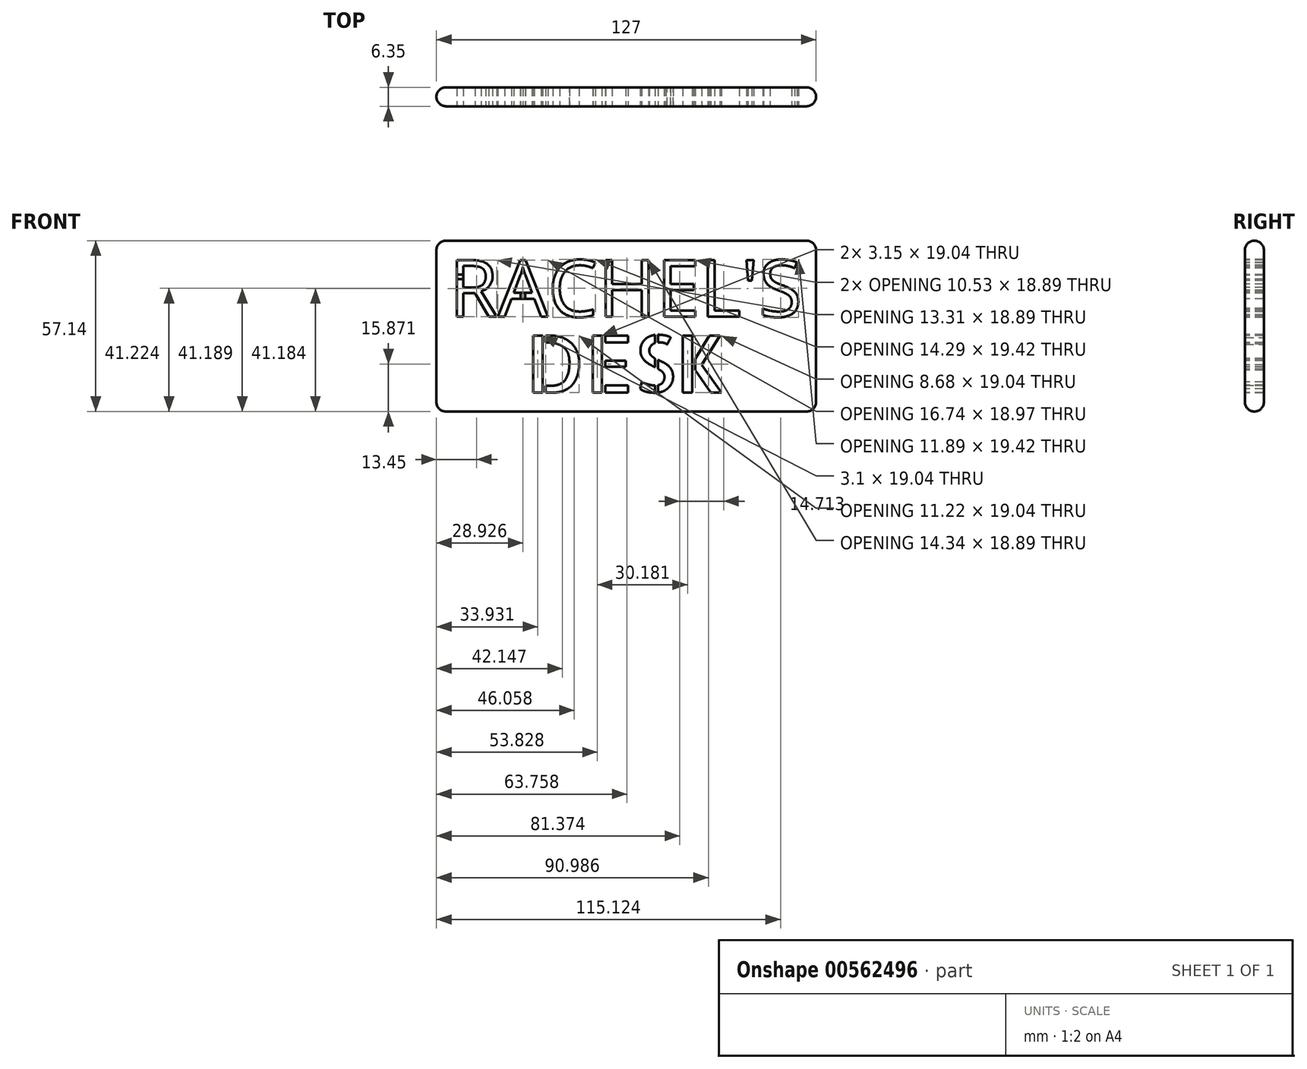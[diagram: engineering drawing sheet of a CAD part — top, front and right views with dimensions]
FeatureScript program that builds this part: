
annotation { "Feature Type Name" : "Feature", "Feature Type Description" : "" }
export const myFeature = defineFeature(function(context is Context, id is Id, definition is map)
    precondition{}
    {
        {
            var Q0;
            Q0=qCreatedBy(makeId("Front.planeOp"),FACE);
            var sketch = newSketch(context, id + "F0", { "sketchPlane" : qUnion([Q0])});
            skLineSegment(sketch, "E0.bottom", {"start": v(-63.5, 28.58) * mm, "end": v(63.5, 28.58) * mm});
            skLineSegment(sketch, "E0.top", {"start": v(-63.5, -28.57) * mm, "end": v(63.5, -28.58) * mm});
            skLineSegment(sketch, "E0.left", {"start": v(-63.5, 28.58) * mm, "end": v(-63.5, -28.58) * mm});
            skLineSegment(sketch, "E0.right", {"start": v(63.5, 28.58) * mm, "end": v(63.5, -28.58) * mm});
            skSolve(sketch);
        }
        {
            var Q0;
            Q0 = qSketchRegion(id + "F0", true);
            extrude(context, id + "F1", {"entities" : qUnion([Q0]), "depth" : 6.35 * mm, "offsetDistance" : 25.4 * mm});
        }
        {
            var Q0;
            Q0=makeQuery(id+"F1.opExtrude","CAP_FACE",FACE,{"disambiguationData":[OSD([sQuery(id+"F0.wireOp",EDGE,"E0.bottom"),sQuery(id+"F0.wireOp",EDGE,"E0.top"),sQuery(id+"F0.wireOp",EDGE,"E0.left"),sQuery(id+"F0.wireOp",EDGE,"E0.right")])],"isStart":false});
            var sketch = newSketch(context, id + "F2", { "sketchPlane" : qUnion([Q0])});
            skText(sketch, "E1", { "text": "RACHEL\'S", "fontName": "OpenSans-Regular.ttf"});
            skText(sketch, "E2", { "text": "DESK", "fontName": "AllertaStencil-Regular.ttf"});
            const initialGuessF2  = {"E1": [-0.0593, 0.00317, 1, 0, 0.01905], "E2": [-0.0336, -0.02222, 1, 0, 0.01905]};
            skSetInitialGuess(sketch, initialGuessF2);
            skSolve(sketch);
        }
        {
            var Q0;
            Q0 = qSketchRegion(id + "F2", true);
            extrude(context, id + "F3", {"entities" : qUnion([Q0]), "operationType" : NewBodyOperationType.REMOVE, "endBound" : BoundingType.THROUGH_ALL, "oppositeDirection" : true, "depth" : 25.4 * mm, "offsetDistance" : 25.4 * mm});
        }
        {
            var Q0;
            {var subQ0=sQuery(id+"F0.wireOp",EDGE,"E0.left");var subQ1=sQuery(id+"F0.wireOp",EDGE,"E0.bottom");var subQ2=sQuery(id+"F0.wireOp",EDGE,"E0.right");var subQ3=sQuery(id+"F0.wireOp",EDGE,"E0.top");Q0=makeQuery(id+"F3.boolean.opBoolean","SPLIT",FACE,{"disambiguationData":[TD([makeQuery(id+"F1.opExtrude","SWEPT_FACE",FACE,{"disambiguationData":[OSD([subQ1])]})])],"derivedFrom":makeQuery(id+"F1.opExtrude","CAP_FACE",FACE,{"disambiguationData":[OSD([subQ1,subQ3,subQ0,subQ2])],"isStart":false})});}
            var sketch = newSketch(context, id + "F4", { "sketchPlane" : qUnion([Q0])});
            skLineSegment(sketch, "E3.bottom", {"start": v(-35.32, 11.16) * mm, "end": v(-33.8, 11.16) * mm});
            skLineSegment(sketch, "E3.top", {"start": v(-35.32, 9.18) * mm, "end": v(-33.8, 9.18) * mm});
            skLineSegment(sketch, "E3.left", {"start": v(-35.32, 11.16) * mm, "end": v(-35.32, 9.18) * mm});
            skLineSegment(sketch, "E3.right", {"start": v(-33.8, 11.16) * mm, "end": v(-33.8, 9.18) * mm});
            skPoint(sketch, "E4", {"position": v(-34.56, 11.16) * mm});
            skPoint(sketch, "E5", {"position": v(-34.56, 9.18) * mm});
            skLineSegment(sketch, "E6.bottom", {"start": v(-56.7, 17.29) * mm, "end": v(-54.5, 17.29) * mm});
            skLineSegment(sketch, "E6.top", {"start": v(-56.7, 15.76) * mm, "end": v(-54.5, 15.76) * mm});
            skLineSegment(sketch, "E6.left", {"start": v(-56.7, 17.29) * mm, "end": v(-56.7, 15.76) * mm});
            skLineSegment(sketch, "E6.right", {"start": v(-54.5, 17.29) * mm, "end": v(-54.5, 15.76) * mm});
            skPoint(sketch, "E7", {"position": v(-54.5, 16.53) * mm});
            skLineSegment(sketch, "E8", {"start": v(-47.03, 17.29) * mm, "end": v(-44.74, 17.29) * mm});
            skLineSegment(sketch, "E9", {"start": v(-47.06, 15.76) * mm, "end": v(-44.79, 15.76) * mm});
            skFitSpline(sketch, "E10.0", {"points": [v(-47, 16.61) * mm, v(-47, 18.48) * mm, v(-48.1, 19.31) * mm]});
            skFitSpline(sketch, "E11.0", {"points": [v(-48.08, 13.84) * mm, v(-47, 14.76) * mm, v(-47, 16.61) * mm]});
            skFitSpline(sketch, "E12.0", {"points": [v(-46.38, 20.73) * mm, v(-44.72, 19.4) * mm, v(-44.72, 16.73) * mm]});
            skFitSpline(sketch, "E13.0", {"points": [v(-44.72, 16.73) * mm, v(-44.72, 12.98) * mm, v(-48.52, 11.66) * mm]});
            skPoint(sketch, "E14.orphan", {"position": v(-46.38, 20.73) * mm});
            skPoint(sketch, "E15.orphan", {"position": v(-48.52, 11.66) * mm});
            skPoint(sketch, "E16.orphan", {"position": v(-48.08, 13.84) * mm});
            skPoint(sketch, "E17.orphan", {"position": v(-48.1, 19.31) * mm});
            skSolve(sketch);
        }
        {
            var Q0;
            Q0 = qSketchRegion(id + "F4", true);
            var Q1;
            Q1=makeQuery(id+"F1.opExtrude","CAP_VERTEX",VERTEX,{"disambiguationData":[OSD([sQuery(id+"F0.wireOp",EDGE,"E0.bottom"),sQuery(id+"F0.wireOp",EDGE,"E0.left")])],"isStart":true});
            extrude(context, id + "F5", {"entities" : qUnion([Q0]), "endBound" : BoundingType.UP_TO_VERTEX, "oppositeDirection" : true, "depth" : 25.4 * mm, "endBoundEntityVertex" : qUnion([Q1]), "offsetDistance" : 25.4 * mm});
        }
        {
            var Q0;
            Q0=makeQuery(id+"F1.opExtrude","CAP_EDGE",EDGE,{"disambiguationData":[OSD([sQuery(id+"F0.wireOp",EDGE,"E0.top")])],"isStart":false});
            var Q1;
            Q1=makeQuery(id+"F1.opExtrude","CAP_EDGE",EDGE,{"disambiguationData":[OSD([sQuery(id+"F0.wireOp",EDGE,"E0.top")])],"isStart":true});
            var Q2;
            Q2=makeQuery(id+"F1.opExtrude","CAP_EDGE",EDGE,{"disambiguationData":[OSD([sQuery(id+"F0.wireOp",EDGE,"E0.left")])],"isStart":false});
            var Q3;
            Q3=makeQuery(id+"F1.opExtrude","CAP_EDGE",EDGE,{"disambiguationData":[OSD([sQuery(id+"F0.wireOp",EDGE,"E0.left")])],"isStart":true});
            var Q4;
            Q4=makeQuery(id+"F1.opExtrude","SWEPT_EDGE",EDGE,{"disambiguationData":[OSD([sQuery(id+"F0.wireOp",EDGE,"E0.top"),sQuery(id+"F0.wireOp",EDGE,"E0.left")])]});
            var Q5;
            Q5=makeQuery(id+"F1.opExtrude","SWEPT_EDGE",EDGE,{"disambiguationData":[OSD([sQuery(id+"F0.wireOp",EDGE,"E0.bottom"),sQuery(id+"F0.wireOp",EDGE,"E0.left")])]});
            var Q6;
            Q6=makeQuery(id+"F1.opExtrude","CAP_EDGE",EDGE,{"disambiguationData":[OSD([sQuery(id+"F0.wireOp",EDGE,"E0.bottom")])],"isStart":false});
            var Q7;
            Q7=makeQuery(id+"F1.opExtrude","CAP_EDGE",EDGE,{"disambiguationData":[OSD([sQuery(id+"F0.wireOp",EDGE,"E0.bottom")])],"isStart":true});
            var Q8;
            Q8=makeQuery(id+"F1.opExtrude","SWEPT_EDGE",EDGE,{"disambiguationData":[OSD([sQuery(id+"F0.wireOp",EDGE,"E0.bottom"),sQuery(id+"F0.wireOp",EDGE,"E0.right")])]});
            var Q9;
            Q9=makeQuery(id+"F1.opExtrude","CAP_EDGE",EDGE,{"disambiguationData":[OSD([sQuery(id+"F0.wireOp",EDGE,"E0.right")])],"isStart":true});
            var Q10;
            Q10=makeQuery(id+"F1.opExtrude","CAP_EDGE",EDGE,{"disambiguationData":[OSD([sQuery(id+"F0.wireOp",EDGE,"E0.right")])],"isStart":false});
            var Q11;
            Q11=makeQuery(id+"F1.opExtrude","SWEPT_EDGE",EDGE,{"disambiguationData":[OSD([sQuery(id+"F0.wireOp",EDGE,"E0.top"),sQuery(id+"F0.wireOp",EDGE,"E0.right")])]});
            fillet(context, id + "F6", {"entities" : qUnion([Q0, Q1, Q2, Q3, Q4, Q5, Q6, Q7, Q8, Q9, Q10, Q11]), "radius" : 3.17 * mm, "tangentPropagation" : true, "allowEdgeOverflow" : false});
        }
    });
